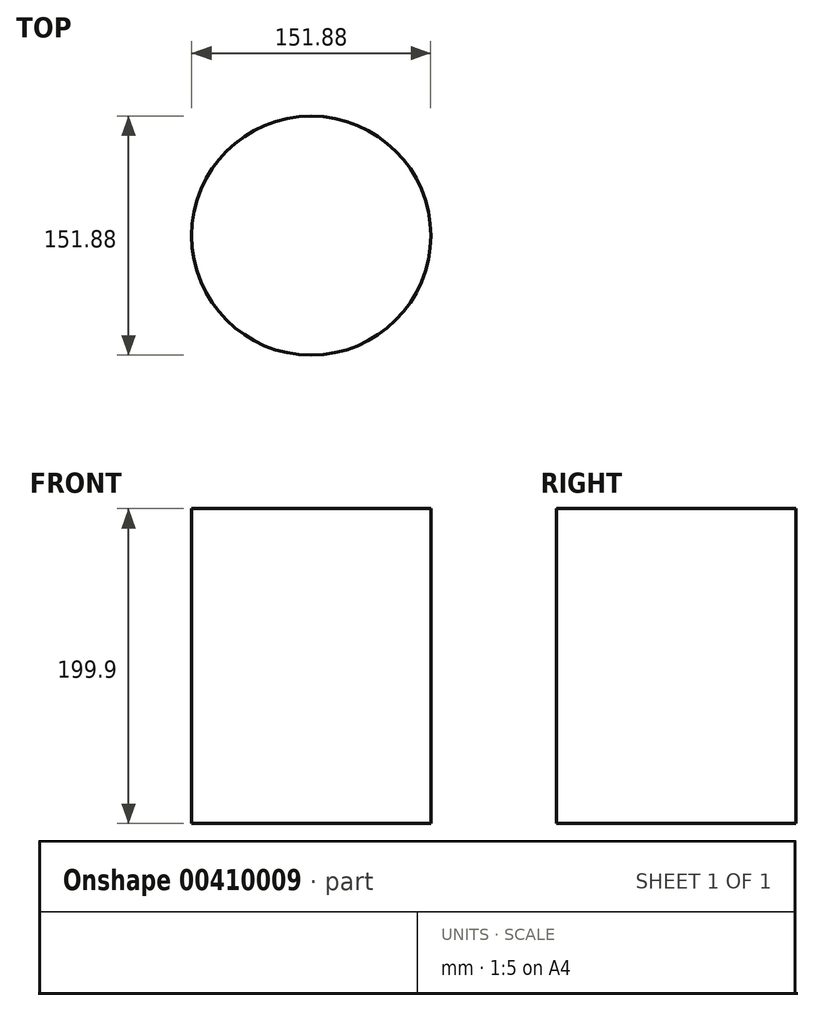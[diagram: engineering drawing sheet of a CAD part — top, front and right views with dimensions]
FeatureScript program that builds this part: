
annotation { "Feature Type Name" : "Feature", "Feature Type Description" : "" }
export const myFeature = defineFeature(function(context is Context, id is Id, definition is map)
    precondition{}
    {
        {
            var Q0;
            Q0=qCreatedBy(makeId("Top.planeOp"),FACE);
            var sketch = newSketch(context, id + "F0", { "sketchPlane" : qUnion([Q0])});
            skCircle(sketch, "E0", {"center": v(0, 0) * mm, "radius": 75.94 * mm});
            skSolve(sketch);
        }
        {
            var Q0;
            Q0=makeQuery(id+"F0.imprint","IMPRINT",FACE,{"disambiguationData":[TD([[makeQuery(id+"F0.imprint","IMPRINT",EDGE,{"derivedFrom":sQuery(id+"F0.wireOp",EDGE,"E0")}),1.0]])]});
            extrude(context, id + "F1", {"entities" : qUnion([Q0]), "depth" : 199.9 * mm});
        }
    });
